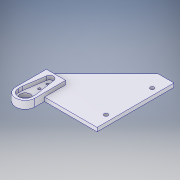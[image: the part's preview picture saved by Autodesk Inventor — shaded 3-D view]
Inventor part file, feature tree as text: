
AUTODESK INVENTOR PART (.ipt)
format: ipt  version: 2017 (Build 210142000, 142)  size: 161,280 bytes
history: native  units: in
note: dims shown in document units (in); Inventor stores cm internally (conversion verified against a paired STEP export)
features: extrude x2, sketch x2, projected_geometry x1
ambient origin geometry x8: Origin, YZ Plane, XZ Plane, XY Plane, X Axis, Y Axis, Z Axis, Center Point
bodies: Solid1 (feature_tree)
feature tree (5):
  extrude  "Extrusion1"  TaperAngle=90.0deg  [1 undecoded]
  extrude  "Extrusion3"  Depth=1.6142in
  sketch  "Sketch3"  dims[d6=2.3622in d7=90.0deg]
  sketch  "Sketch6"  dims[d8=0.4929in d9=1.6142in d10=0.2953in d11=0.5906in d13=0.9456in d14=0.1181in d15=0.0in d18=0.1969in d19=0.4724in d20=0.4724in d21=0.1181in d22=0.1181in d25=0.315in d26=0.4335in d27=0.2562in d28=0.0787in d29=0.0787in d31=0.4331in d32=0.0591in d33=0.2362in d34=0.1181in d35=0.1181in d36=0.0in]
  projected_geometry  "Projected Loop3"
note: 1 required parameter value undecoded (feature->parameter linkage not recoverable at this tier; creation-order binding heuristic only, values carry confidence <= 0.55)
